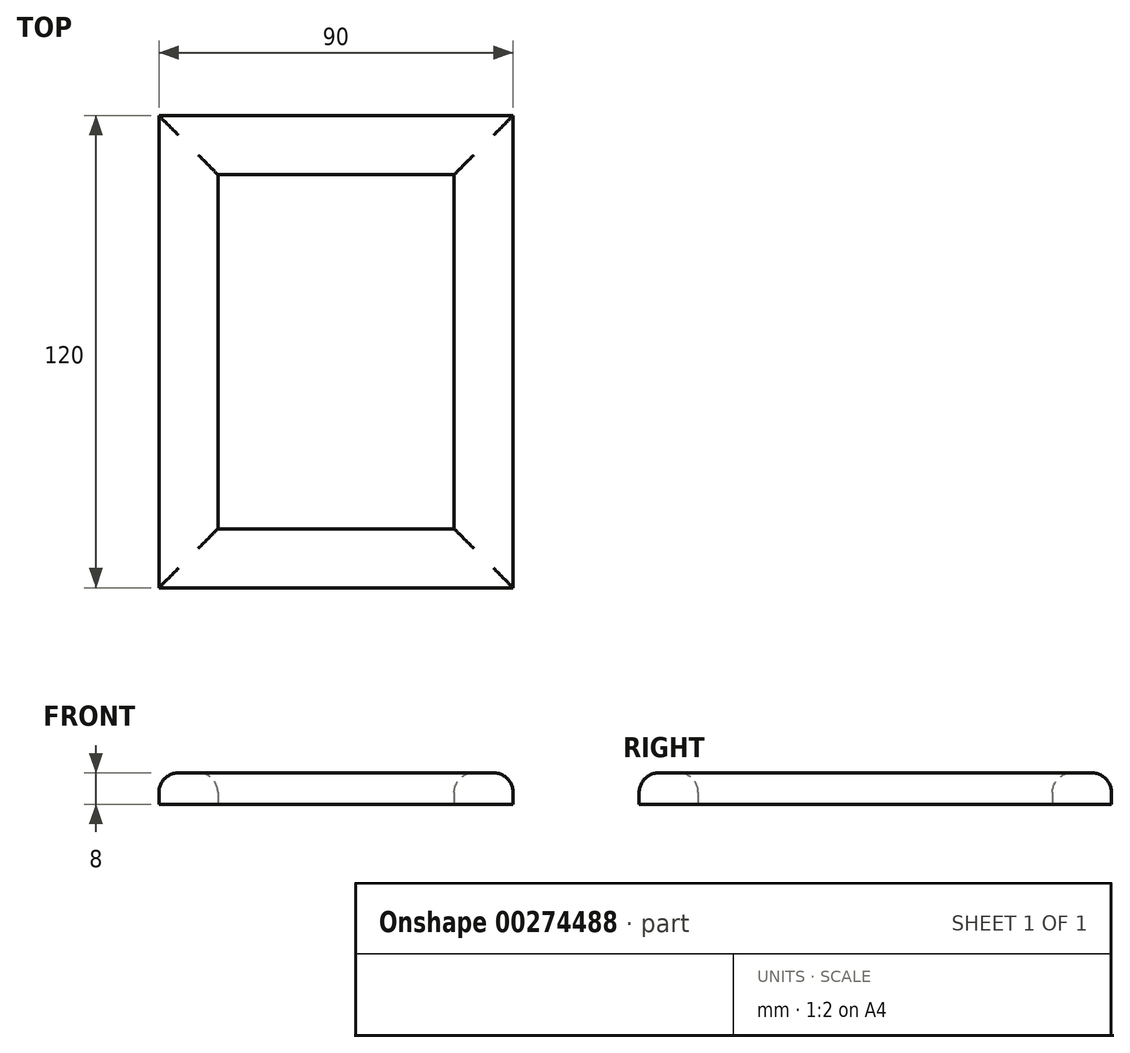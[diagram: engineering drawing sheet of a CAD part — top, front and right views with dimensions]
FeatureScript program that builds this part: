
annotation { "Feature Type Name" : "Feature", "Feature Type Description" : "" }
export const myFeature = defineFeature(function(context is Context, id is Id, definition is map)
    precondition{}
    {
        {
            var Q0;
            Q0=qCreatedBy(makeId("Top.planeOp"),FACE);
            var sketch = newSketch(context, id + "F0", { "sketchPlane" : qUnion([Q0])});
            skLineSegment(sketch, "E0.bottom", {"start": v(30, -45) * mm, "end": v(-30, -45) * mm});
            skLineSegment(sketch, "E0.top", {"start": v(30, 45) * mm, "end": v(-30, 45) * mm});
            skLineSegment(sketch, "E0.left", {"start": v(30, -45) * mm, "end": v(30, 45) * mm});
            skLineSegment(sketch, "E0.right", {"start": v(-30, -45) * mm, "end": v(-30, 45) * mm});
            skPoint(sketch, "E0.middle", {"position": v(0, 0) * mm});
            skLineSegment(sketch, "E1.bottom", {"start": v(45, -60) * mm, "end": v(-45, -60) * mm});
            skLineSegment(sketch, "E1.top", {"start": v(45, 60) * mm, "end": v(-45, 60) * mm});
            skLineSegment(sketch, "E1.left", {"start": v(45, -60) * mm, "end": v(45, 60) * mm});
            skLineSegment(sketch, "E1.right", {"start": v(-45, -60) * mm, "end": v(-45, 60) * mm});
            skLineSegment(sketch, "E2.bottom", {"start": v(40, -55) * mm, "end": v(-40, -55) * mm});
            skLineSegment(sketch, "E2.top", {"start": v(40, 55) * mm, "end": v(-40, 55) * mm});
            skLineSegment(sketch, "E2.left", {"start": v(40, -55) * mm, "end": v(40, 55) * mm});
            skLineSegment(sketch, "E2.right", {"start": v(-40, -55) * mm, "end": v(-40, 55) * mm});
            skSolve(sketch);
        }
        {
            var Q0;
            Q0=makeQuery(id+"F0.imprint","IMPRINT",FACE,{"disambiguationData":[TD([[makeQuery(id+"F0.imprint","IMPRINT",EDGE,{"derivedFrom":sQuery(id+"F0.wireOp",EDGE,"E1.bottom")}),-1.0]])]});
            var Q1;
            Q1=makeQuery(id+"F0.imprint","IMPRINT",FACE,{"disambiguationData":[TD([[makeQuery(id+"F0.imprint","IMPRINT",EDGE,{"derivedFrom":sQuery(id+"F0.wireOp",EDGE,"E0.bottom")}),1.0]])]});
            extrude(context, id + "F1", {"entities" : qUnion([Q0, Q1]), "depth" : 8 * mm});
        }
        {
            var Q0;
            Q0=makeQuery(id+"F1.opExtrude","CAP_FACE",FACE,{"disambiguationData":[OSD([sQuery(id+"F0.wireOp",EDGE,"E0.bottom"),sQuery(id+"F0.wireOp",EDGE,"E0.top"),sQuery(id+"F0.wireOp",EDGE,"E0.left"),sQuery(id+"F0.wireOp",EDGE,"E0.right"),sQuery(id+"F0.wireOp",EDGE,"E1.bottom"),sQuery(id+"F0.wireOp",EDGE,"E1.top"),sQuery(id+"F0.wireOp",EDGE,"E1.left"),sQuery(id+"F0.wireOp",EDGE,"E1.right")])],"isStart":false});
            fillet(context, id + "F2", {"entities" : qUnion([Q0]), "radius" : 5 * mm, "tangentPropagation" : true, "allowEdgeOverflow" : false});
        }
    });
